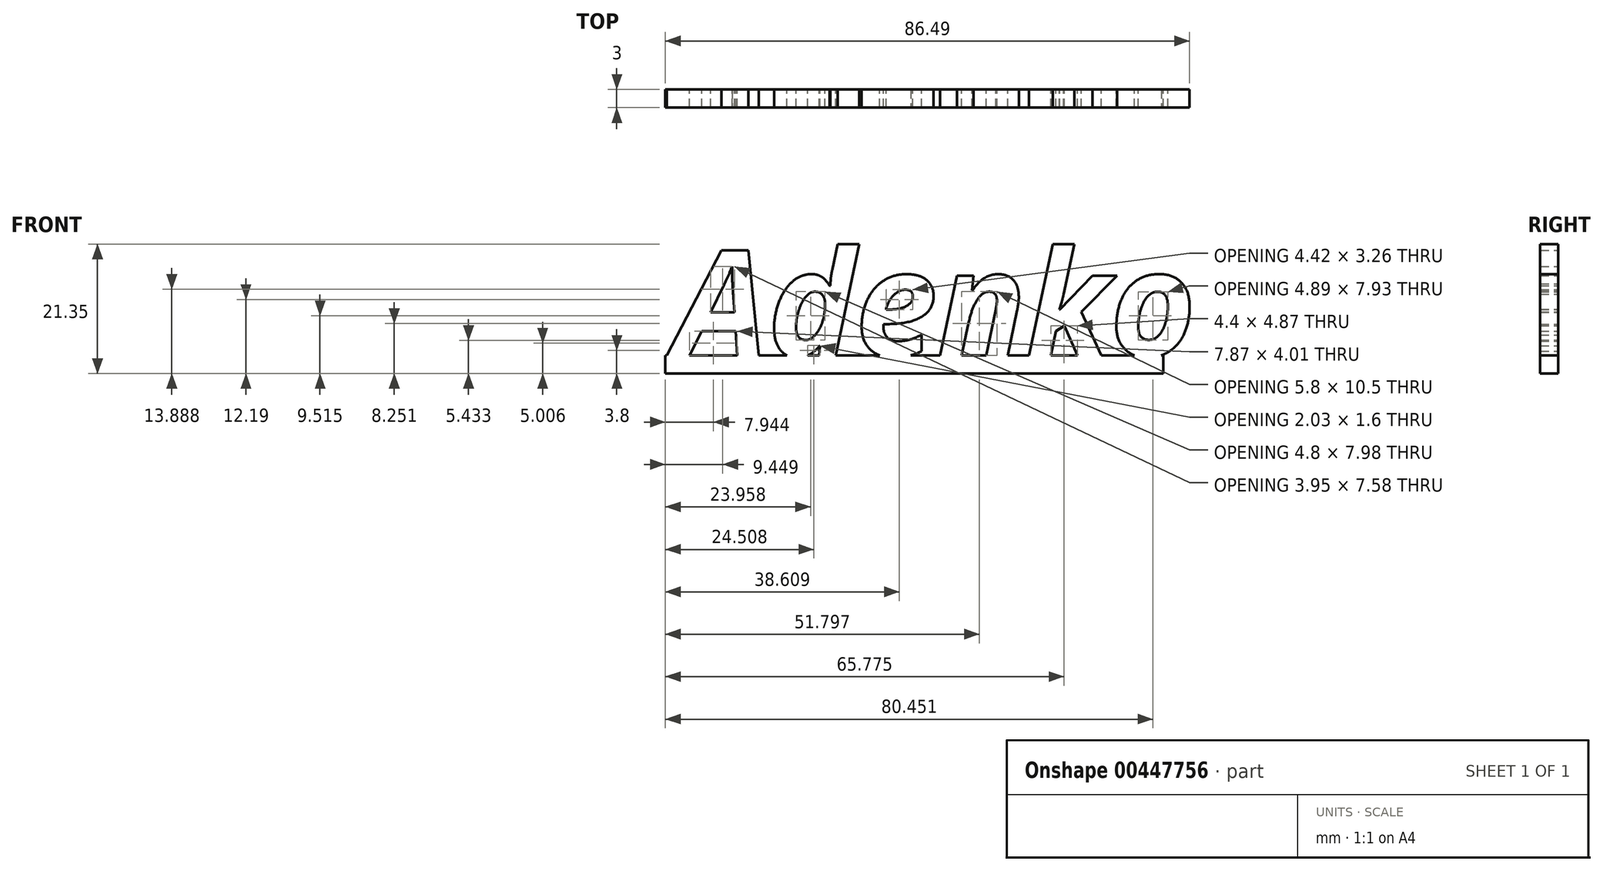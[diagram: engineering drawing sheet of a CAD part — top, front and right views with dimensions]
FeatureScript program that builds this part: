
annotation { "Feature Type Name" : "Feature", "Feature Type Description" : "" }
export const myFeature = defineFeature(function(context is Context, id is Id, definition is map)
    precondition{}
    {
        {
            var Q0;
            Q0=qCreatedBy(makeId("Front.planeOp"),FACE);
            var sketch = newSketch(context, id + "F0", { "sketchPlane" : qUnion([Q0])});
            skLineSegment(sketch, "E0.bottom", {"start": v(-46.36, 0) * mm, "end": v(35.81, 0) * mm});
            skLineSegment(sketch, "E0.top", {"start": v(-46.36, -3) * mm, "end": v(35.81, -3) * mm});
            skLineSegment(sketch, "E0.left", {"start": v(-46.36, 0) * mm, "end": v(-46.36, -3) * mm});
            skLineSegment(sketch, "E0.right", {"start": v(35.81, 0) * mm, "end": v(35.81, -3) * mm});
            skText(sketch, "E1", { "text": "Adenko", "fontName": "OpenSans-BoldItalic.ttf"});
            const initialGuessF0  = {"E1": [-0.04475, -0.00012, 1, 0, 0.0175]};
            skSetInitialGuess(sketch, initialGuessF0);
            skSolve(sketch);
        }
        {
            var Q0;
            Q0=qSketchRegion(id+"F0",true);
            extrude(context, id + "F1", {"entities" : qUnion([Q0]), "depth" : 3 * mm});
        }
    });
